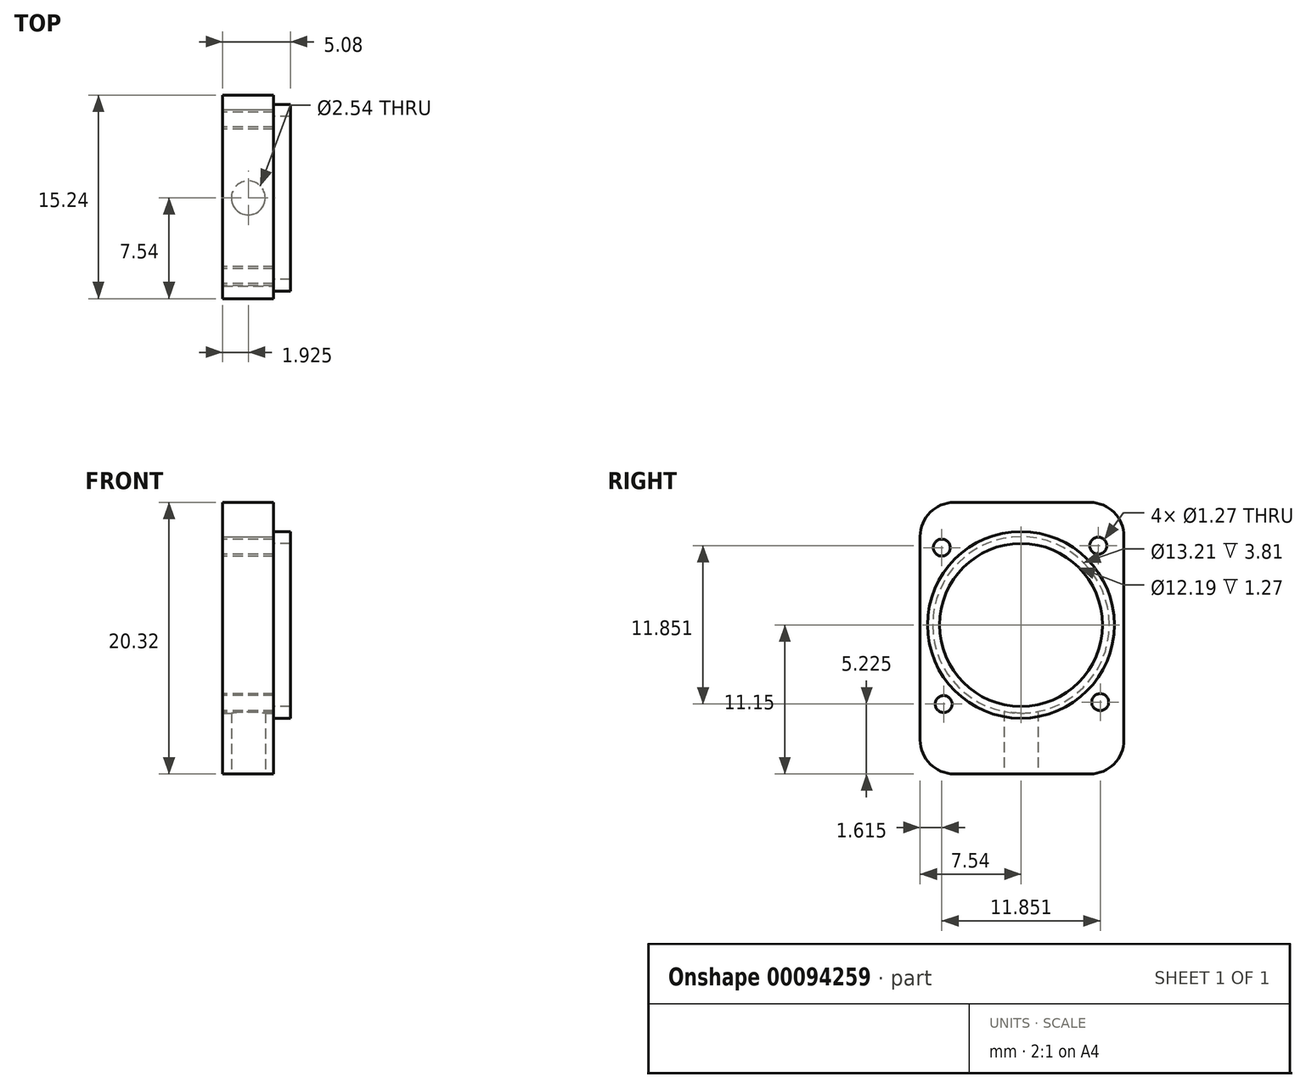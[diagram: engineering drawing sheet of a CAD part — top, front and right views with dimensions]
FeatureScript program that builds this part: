
annotation { "Feature Type Name" : "Feature", "Feature Type Description" : "" }
export const myFeature = defineFeature(function(context is Context, id is Id, definition is map)
    precondition{}
    {
        {
            var Q0;
            Q0=qCreatedBy(makeId("Right.planeOp"),FACE);
            var sketch = newSketch(context, id + "F0", { "sketchPlane" : qUnion([Q0])});
            skPoint(sketch, "E0.visualSharp", {"position": v(7.52, -7.48) * mm});
            skCircle(sketch, "E1", {"center": v(0, 0) * mm, "radius": 6.1 * mm});
            skCircle(sketch, "E2", {"center": v(0, 0) * mm, "radius": 6.99 * mm});
            skSolve(sketch);
        }
        {
            var Q0;
            Q0=makeQuery(id+"F0.imprint","IMPRINT",FACE,{"disambiguationData":[TD([[makeQuery(id+"F0.imprint","IMPRINT",EDGE,{"derivedFrom":sQuery(id+"F0.wireOp",EDGE,"Uzbq3elM-GcDj-fcVd-HrAi-XYye0wBE9Fp0.bottom")}),-1.0]])]});
            var Q1;
            Q1 = qSketchRegion(id + "F2", true);
            var Q2;
            Q2=makeQuery(id+"F0.imprint","IMPRINT",FACE,{"disambiguationData":[TD([[makeQuery(id+"F0.imprint","IMPRINT",EDGE,{"derivedFrom":sQuery(id+"F0.wireOp",EDGE,"E1")}),-1.0]])]});
            extrude(context, id + "F1", {"entities" : qUnion([Q0, Q1, Q2]), "depth" : 1.27 * mm});
        }
        {
            var Q0;
            Q0=qCreatedBy(makeId("Right.planeOp"),FACE);
            var sketch = newSketch(context, id + "F2", { "sketchPlane" : qUnion([Q0])});
            skLineSegment(sketch, "E3.bottom", {"start": v(-5, 9.17) * mm, "end": v(5.16, 9.17) * mm});
            skLineSegment(sketch, "E3.top", {"start": v(-5, -11.15) * mm, "end": v(5.16, -11.15) * mm});
            skLineSegment(sketch, "E3.left", {"start": v(-7.54, 6.63) * mm, "end": v(-7.54, -8.61) * mm});
            skLineSegment(sketch, "E3.right", {"start": v(7.7, 6.63) * mm, "end": v(7.7, -8.61) * mm});
            skPoint(sketch, "E4.visualSharp", {"position": v(-7.54, 9.17) * mm});
            skArc(sketch, "E4.filletArc", {"start": v(-5, 9.17) * mm, "mid": v(-6.8, 8.42) * mm, "end": v(-7.54, 6.63) * mm});
            skArc(sketch, "E5.filletArc", {"start": v(7.7, 6.63) * mm, "mid": v(6.95, 8.42) * mm, "end": v(5.16, 9.17) * mm});
            skPoint(sketch, "E6.visualSharp", {"position": v(7.7, -11.15) * mm});
            skArc(sketch, "E6.filletArc", {"start": v(5.16, -11.15) * mm, "mid": v(6.95, -10.4) * mm, "end": v(7.7, -8.61) * mm});
            skPoint(sketch, "E7.visualSharp", {"position": v(-7.54, -11.15) * mm});
            skArc(sketch, "E7.filletArc", {"start": v(-7.54, -8.61) * mm, "mid": v(-6.8, -10.4) * mm, "end": v(-5, -11.15) * mm});
            skCircle(sketch, "E8", {"center": v(0, 0) * mm, "radius": 6.6 * mm});
            skSolve(sketch);
        }
        {
            var Q0;
            Q0=makeQuery(id+"F2.imprint","IMPRINT",FACE,{"disambiguationData":[TD([[makeQuery(id+"F2.imprint","IMPRINT",EDGE,{"derivedFrom":sQuery(id+"F2.wireOp",EDGE,"E3.bottom")}),-1.0]])]});
            extrude(context, id + "F3", {"entities" : qUnion([Q0]), "operationType" : NewBodyOperationType.ADD, "oppositeDirection" : true, "depth" : 3.8 * mm});
        }
        {
            var Q0;
            Q0=makeQuery(id+"F3.opExtrude","CAP_FACE",FACE,{"disambiguationData":[OSD([sQuery(id+"F2.wireOp",EDGE,"E3.bottom"),sQuery(id+"F2.wireOp",EDGE,"E3.top"),sQuery(id+"F2.wireOp",EDGE,"E3.left"),sQuery(id+"F2.wireOp",EDGE,"E3.right"),sQuery(id+"F2.wireOp",EDGE,"E4.filletArc"),sQuery(id+"F2.wireOp",EDGE,"E5.filletArc"),sQuery(id+"F2.wireOp",EDGE,"E6.filletArc"),sQuery(id+"F2.wireOp",EDGE,"E7.filletArc"),sQuery(id+"F2.wireOp",EDGE,"E8")])],"isStart":false});
            var sketch = newSketch(context, id + "F4", { "sketchPlane" : qUnion([Q0])});
            skCircle(sketch, "E9", {"center": v(-5.78, 5.93) * mm, "radius": 0.64 * mm});
            skCircle(sketch, "E10", {"center": v(5.93, 5.78) * mm, "radius": 0.64 * mm});
            skCircle(sketch, "E11", {"center": v(5.78, -5.93) * mm, "radius": 0.64 * mm});
            skCircle(sketch, "E12", {"center": v(-5.93, -5.78) * mm, "radius": 0.64 * mm});
            skSolve(sketch);
        }
        {
            var Q0;
            Q0=sQuery(id+"F4.wireOp",VERTEX,"E10.center");
            var Q1;
            Q1=sQuery(id+"F4.wireOp",VERTEX,"E9.center");
            var Q2;
            Q2=sQuery(id+"F4.wireOp",VERTEX,"E11.center");
            var Q3;
            Q3=sQuery(id+"F4.wireOp",VERTEX,"E12.center");
            var Q4;
            Q4=makeQuery(id+"F1.opExtrude","SWEPT_BODY",BODY,{"disambiguationData":[OSD([sQuery(id+"F0.wireOp",EDGE,"Uzbq3elM-GcDj-fcVd-HrAi-XYye0wBE9Fp0.bottom"),sQuery(id+"F0.wireOp",EDGE,"Uzbq3elM-GcDj-fcVd-HrAi-XYye0wBE9Fp0.top"),sQuery(id+"F0.wireOp",EDGE,"Uzbq3elM-GcDj-fcVd-HrAi-XYye0wBE9Fp0.left"),sQuery(id+"F0.wireOp",EDGE,"Uzbq3elM-GcDj-fcVd-HrAi-XYye0wBE9Fp0.right"),sQuery(id+"F0.wireOp",EDGE,"c236dfe6-28d2-43dc-b6c5-caf366ad4b72.filletArc"),sQuery(id+"F0.wireOp",EDGE,"6ac6db7e-b89f-4b98-9049-1daa55fbfa09.filletArc"),sQuery(id+"F0.wireOp",EDGE,"E0.filletArc"),sQuery(id+"F0.wireOp",EDGE,"33ecd720-5e03-4470-b49b-3a4d13693ea1.filletArc"),sQuery(id+"F0.wireOp",EDGE,"E1")])]});
            hole(context, id + "F5", {"style" : HoleStyle.SIMPLE, "endStyle" : HoleEndStyle.THROUGH, "holeDiameter" : 1.27 * mm, "locations" : qUnion([Q0, Q1, Q2, Q3]), "scope" : qUnion([Q4]), "isTappedThrough" : true});
        }
        {
            var Q0;
            Q0=makeQuery(id+"F3.opExtrude","SWEPT_FACE",FACE,{"disambiguationData":[OSD([sQuery(id+"F2.wireOp",EDGE,"E3.top")])]});
            var sketch = newSketch(context, id + "F6", { "sketchPlane" : qUnion([Q0])});
            skCircle(sketch, "E13", {"center": v(-1.88, 0) * mm, "radius": 1.27 * mm});
            skSolve(sketch);
        }
        {
            var Q0;
            Q0=sQuery(id+"F6.wireOp",VERTEX,"E13.center");
            var Q1;
            Q1=makeQuery(id+"F1.opExtrude","SWEPT_BODY",BODY,{"disambiguationData":[OSD([sQuery(id+"F0.wireOp",EDGE,"E1"),sQuery(id+"F0.wireOp",EDGE,"E2")])]});
            hole(context, id + "F7", {"style" : HoleStyle.SIMPLE, "endStyle" : HoleEndStyle.BLIND, "holeDiameter" : 2.54 * mm, "holeDepth" : 5.08 * mm, "locations" : qUnion([Q0]), "scope" : qUnion([Q1])});
        }
    });
